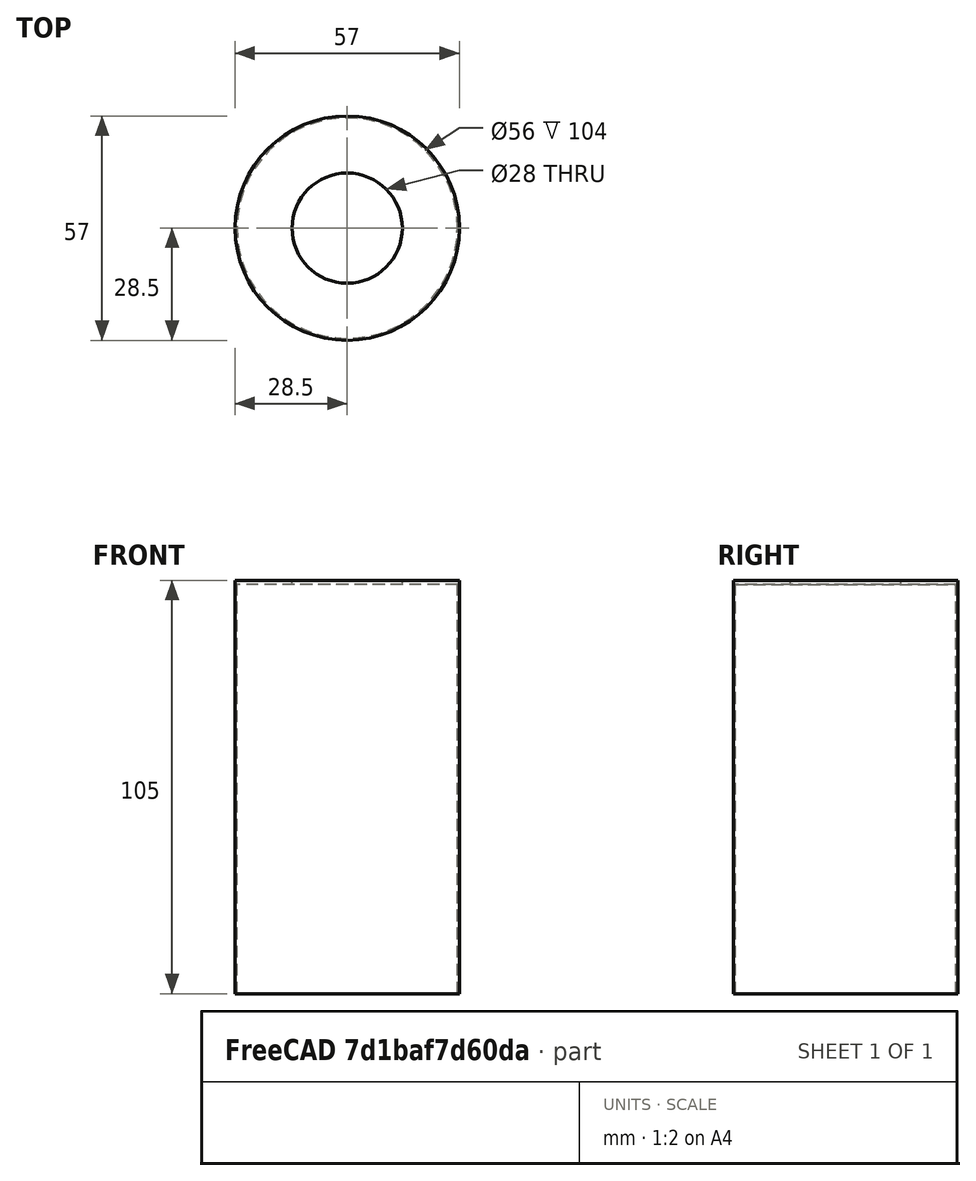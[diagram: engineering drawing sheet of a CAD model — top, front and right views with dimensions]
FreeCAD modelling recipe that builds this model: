
FCSTD DOCUMENT  (FreeCAD 0.19R)
Label: boitier
License: All rights reserved
LicenseURL: http://en.wikipedia.org/wiki/All_rights_reserved
objects: Part::Cylinder×2, Part::Cut×2, Sketcher::SketchObject×1, Part::Extrusion×1
note: 6 computed .brp shape members not serialized (recipe doc carries the construction recipe); baked Part::Feature solids carry a one-line shape summary decoded from their .brp

FEATURE [Sketcher::SketchObject] Sketch
  FullyConstrained = true
  sketch-geometry (1):
    g0: Circle CenterX=0 CenterY=0 CenterZ=0 NormalX=0 NormalY=0 NormalZ=1 AngleXU=0 Radius=28.5
  constraints (2):
    c: Coincident(g0,g-1)
    c: Diameter(g0) = 57
FEATURE [Part::Extrusion] Extrude
  Base = -> Sketch
  Dir = (0,0,1)
  DirMode = 2
  FaceMakerClass = Part::FaceMakerBullseye
  LengthFwd = 105
  LengthRev = 0
  Solid = true
  Symmetric = false
FEATURE [Part::Cylinder] Cylinder
  Angle = 360
  AttacherType = Attacher::AttachEngine3D
  Height = 104
  Radius = 28
FEATURE [Part::Cut] Cut
  Base = -> Extrude
  Tool = -> Cylinder
FEATURE [Part::Cylinder] Cylinder001
  Angle = 360
  AttacherType = Attacher::AttachEngine3D
  Height = 110
  Radius = 14
FEATURE [Part::Cut] Cut001
  Base = -> Cut
  Tool = -> Cylinder001
